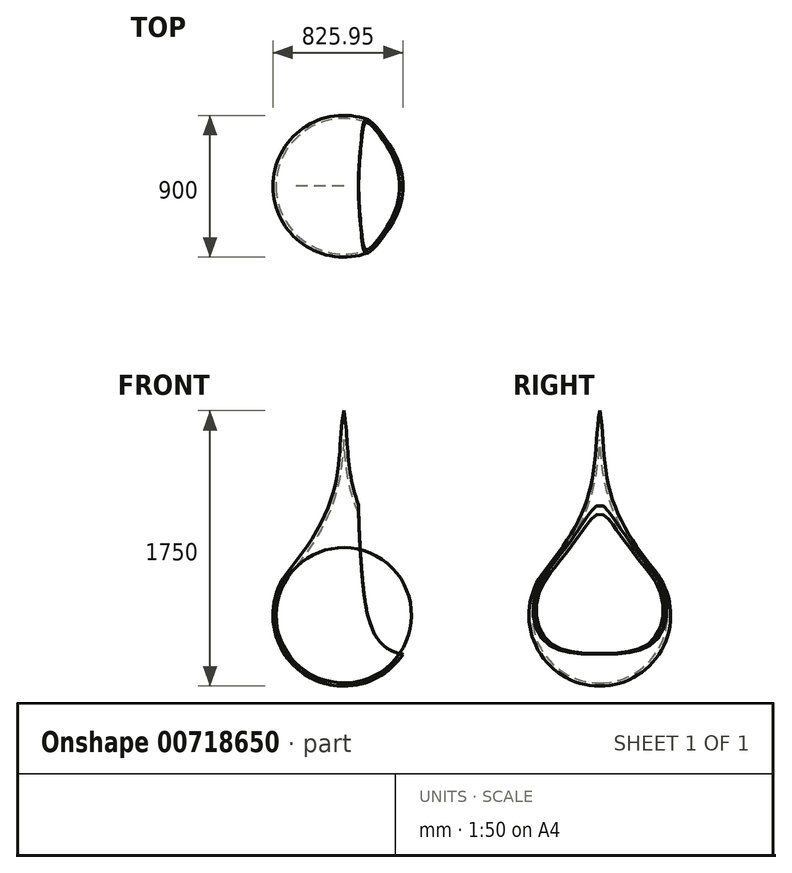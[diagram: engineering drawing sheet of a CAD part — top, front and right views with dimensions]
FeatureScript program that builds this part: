
annotation { "Feature Type Name" : "Feature", "Feature Type Description" : "" }
export const myFeature = defineFeature(function(context is Context, id is Id, definition is map)
    precondition{}
    {
        {
            var Q0;
            Q0=qCreatedBy(makeId("Front.planeOp"),FACE);
            var sketch = newSketch(context, id + "F0", { "sketchPlane" : qUnion([Q0])});
            skArc(sketch, "E0", {"start": v(-348.76, 284.36) * mm, "mid": v(-406.49, -193.05) * mm, "end": v(0, -450) * mm});
            skFitSpline(sketch, "E1", {"points": [v(0, 1300) * mm, v(-111.1, 656.4) * mm, v(-1268.78, -572.09) * mm], "startDerivative": vector(-267.92, -1340.5) * mm, "endDerivative": vector(-2252.95, -1776.73) * mm});
            skLineSegment(sketch, "E2", {"start": v(0, 1300) * mm, "end": v(0, -450) * mm});
            skSolve(sketch);
        }
        {
            var Q0;
            Q0 = qSketchRegion(id + "F0", true);
            var Q1;
            Q1=sQuery(id+"F0.wireOp",EDGE,"E2");
            revolve(context, id + "F1", {"surfaceOperationType" : NewSurfaceOperationType.NEW, "entities" : qUnion([Q0]), "axis" : qUnion([Q1]), "revolveType" : RevolveType.FULL});
        }
        {
            var Q0;
            Q0=qCreatedBy(makeId("Front.planeOp"),FACE);
            var sketch = newSketch(context, id + "F2", { "sketchPlane" : qUnion([Q0])});
            skFitSpline(sketch, "E3", {"points": [v(91.77, 1144.62) * mm, v(116.57, 252.52) * mm, v(273.7, -209.73) * mm, v(872.99, -276.1) * mm], "startDerivative": vector(-24.61, -3540.98) * mm, "endDerivative": vector(2039.92, -461.94) * mm});
            skLineSegment(sketch, "E4", {"start": v(872.99, -276.1) * mm, "end": v(91.77, 1144.62) * mm});
            skSolve(sketch);
        }
        {
            var Q0;
            Q0 = qSketchRegion(id + "F2", true);
            extrude(context, id + "F3", {"entities" : qUnion([Q0]), "operationType" : NewBodyOperationType.REMOVE, "endBound" : BoundingType.SYMMETRIC, "oppositeDirection" : true, "depth" : 1200 * mm, "offsetDistance" : 25 * mm});
        }
        {
            var Q0;
            Q0=makeQuery(id+"F3.boolean.opBoolean","COPY",FACE,{"derivedFrom":makeQuery(id+"F3.opExtrude","SWEPT_FACE",FACE,{"disambiguationData":[OSD([sQuery(id+"F2.wireOp",EDGE,"E3")])]})});
            shell(context, id + "F4", {"entities" : qUnion([Q0]), "thickness" : 20 * mm});
        }
    });
